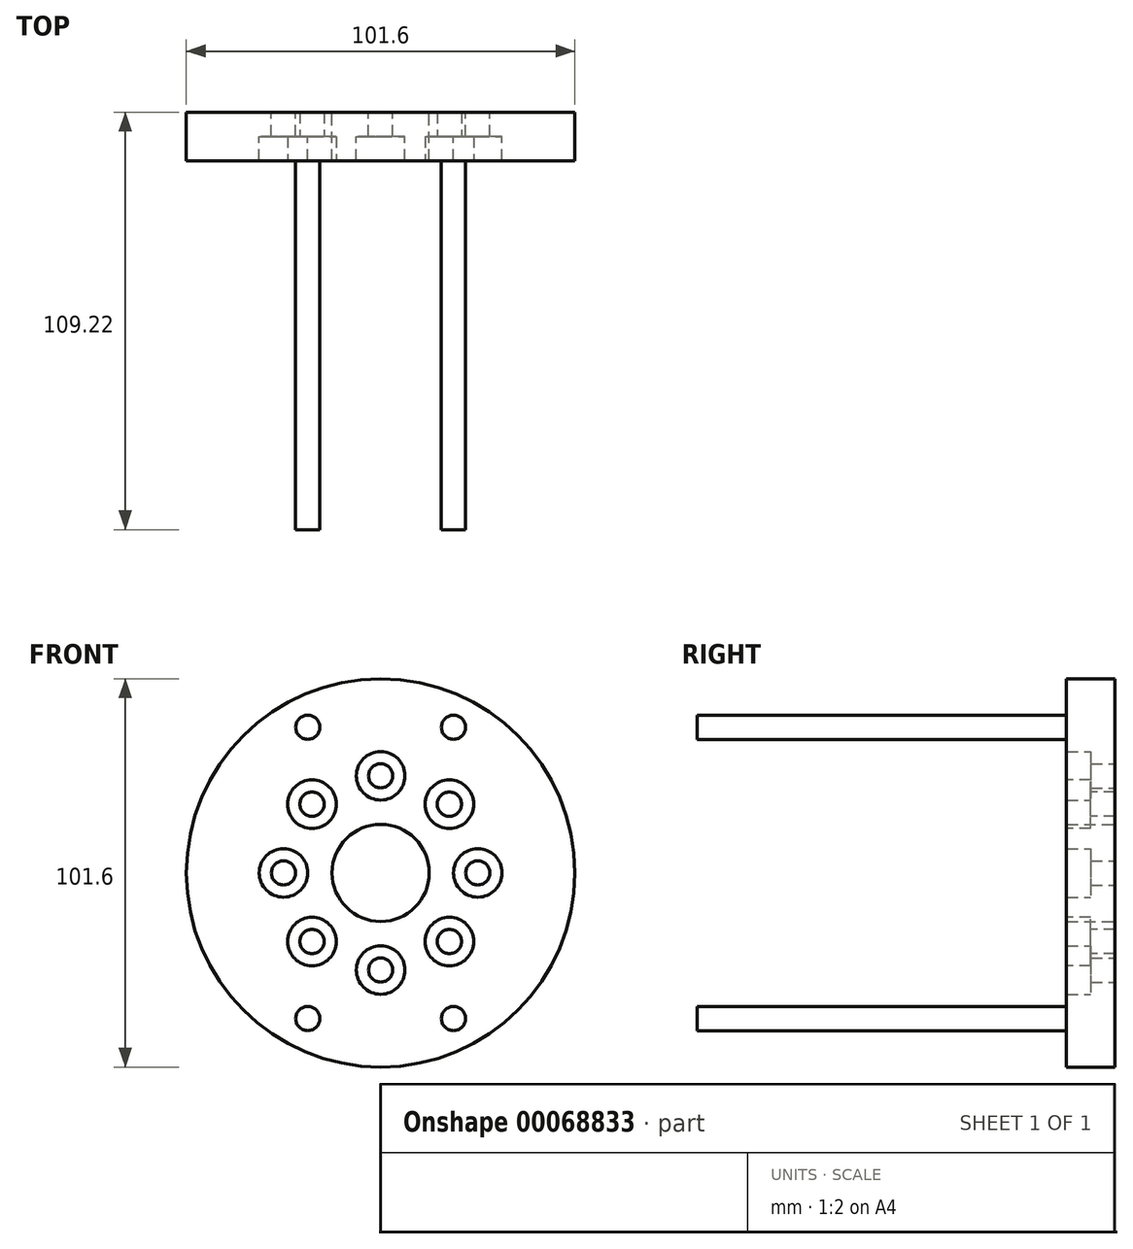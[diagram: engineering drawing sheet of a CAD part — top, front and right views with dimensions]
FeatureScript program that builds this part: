
annotation { "Feature Type Name" : "Feature", "Feature Type Description" : "" }
export const myFeature = defineFeature(function(context is Context, id is Id, definition is map)
    precondition{}
    {
        {
            var Q0;
            Q0=qCreatedBy(makeId("Front.planeOp"),FACE);
            var sketch = newSketch(context, id + "F0", { "sketchPlane" : qUnion([Q0])});
            skCircle(sketch, "E0", {"center": v(0, 0) * mm, "radius": 50.8 * mm});
            skCircle(sketch, "E1", {"center": v(0, 0) * mm, "radius": 12.7 * mm});
            skCircle(sketch, "E2", {"center": v(0, 0) * mm, "radius": 34.93 * mm, "construction": true});
            skPoint(sketch, "E3", {"position": v(0, 34.93) * mm});
            skPoint(sketch, "E4", {"position": v(-34.93, 0) * mm});
            skPoint(sketch, "E5", {"position": v(0, -34.92) * mm});
            skPoint(sketch, "E6", {"position": v(34.93, 0) * mm});
            skSolve(sketch);
        }
        {
            var Q0;
            Q0 = qSketchRegion(id + "F0", true);
            extrude(context, id + "F1", {"entities" : qUnion([Q0]), "depth" : 12.7 * mm});
        }
        {
            var Q0;
            Q0=makeQuery(id+"F1.opExtrude","CAP_FACE",FACE,{"disambiguationData":[OSD([sQuery(id+"F0.wireOp",EDGE,"E0")])],"isStart":false});
            var sketch = newSketch(context, id + "F2", { "sketchPlane" : qUnion([Q0])});
            skCircle(sketch, "E7", {"center": v(-17.96, 17.96) * mm, "radius": 6.35 * mm});
            skCircle(sketch, "E8", {"center": v(17.96, 17.96) * mm, "radius": 6.35 * mm});
            skCircle(sketch, "E9", {"center": v(17.96, -17.96) * mm, "radius": 6.35 * mm});
            skCircle(sketch, "E10", {"center": v(-17.96, -17.96) * mm, "radius": 6.35 * mm});
            skCircle(sketch, "E11", {"center": v(0, 0) * mm, "radius": 25.4 * mm, "construction": true});
            skLineSegment(sketch, "E12", {"start": v(0, 0) * mm, "end": v(-17.96, 17.96) * mm, "construction": true});
            skLineSegment(sketch, "E13", {"start": v(0, 0) * mm, "end": v(-25.4, 0) * mm, "construction": true});
            skPoint(sketch, "E14", {"position": v(0, 25.4) * mm});
            skPoint(sketch, "E15", {"position": v(-25.4, 0) * mm});
            skPoint(sketch, "E16", {"position": v(25.4, 0) * mm});
            skPoint(sketch, "E17", {"position": v(0, -25.4) * mm});
            skSolve(sketch);
        }
        {
            var Q0;
            Q0 = qSketchRegion(id + "F2", true);
            extrude(context, id + "F3", {"entities" : qUnion([Q0]), "operationType" : NewBodyOperationType.REMOVE, "oppositeDirection" : true, "depth" : 6.35 * mm});
        }
        {
            var Q0;
            Q0=sQuery(id+"F2.wireOp",VERTEX,"E14");
            var Q1;
            Q1=sQuery(id+"F2.wireOp",VERTEX,"E15");
            var Q2;
            Q2=sQuery(id+"F2.wireOp",VERTEX,"E17");
            var Q3;
            Q3=sQuery(id+"F2.wireOp",VERTEX,"E16");
            var Q4;
            Q4=makeQuery(id+"F1.opExtrude","SWEPT_BODY",BODY,{"disambiguationData":[OSD([sQuery(id+"F0.wireOp",EDGE,"E0"),sQuery(id+"F0.wireOp",EDGE,"E1")])]});
            hole(context, id + "F4", {"style" : HoleStyle.C_BORE, "holeDiameter" : 6.35 * mm, "cBoreDiameter" : 12.7 * mm, "cBoreDepth" : 6.35 * mm, "endStyle" : HoleEndStyle.THROUGH, "locations" : qUnion([Q0, Q1, Q2, Q3]), "scope" : qUnion([Q4])});
        }
        {
            var Q0;
            Q0=makeQuery(id+"F1.opExtrude","CAP_FACE",FACE,{"disambiguationData":[OSD([sQuery(id+"F0.wireOp",EDGE,"E0"),sQuery(id+"F0.wireOp",EDGE,"E1")])],"isStart":false});
            var sketch = newSketch(context, id + "F5", { "sketchPlane" : qUnion([Q0])});
            skCircle(sketch, "E18", {"center": v(-19.05, 38.1) * mm, "radius": 3.18 * mm});
            skCircle(sketch, "E19", {"center": v(19.05, 38.1) * mm, "radius": 3.18 * mm});
            skCircle(sketch, "E20", {"center": v(19.05, -38.1) * mm, "radius": 3.18 * mm});
            skCircle(sketch, "E21", {"center": v(-19.05, -38.1) * mm, "radius": 3.18 * mm});
            skLineSegment(sketch, "E22.bottom", {"start": v(-19.05, -38.1) * mm, "end": v(19.05, -38.1) * mm, "construction": true});
            skLineSegment(sketch, "E22.top", {"start": v(-19.05, 38.1) * mm, "end": v(19.05, 38.1) * mm, "construction": true});
            skLineSegment(sketch, "E22.left", {"start": v(-19.05, -38.1) * mm, "end": v(-19.05, 38.1) * mm, "construction": true});
            skLineSegment(sketch, "E22.right", {"start": v(19.05, -38.1) * mm, "end": v(19.05, 38.1) * mm, "construction": true});
            skSolve(sketch);
        }
        {
            var Q0;
            Q0 = qSketchRegion(id + "F5", true);
            extrude(context, id + "F6", {"entities" : qUnion([Q0]), "operationType" : NewBodyOperationType.ADD, "depth" : 96.52 * mm});
        }
        {
            var Q0;
            Q0=makeQuery(id+"F3.boolean.opBoolean","COPY",FACE,{"derivedFrom":makeQuery(id+"F3.opExtrude","CAP_FACE",FACE,{"disambiguationData":[OSD([sQuery(id+"F2.wireOp",EDGE,"E7")])],"isStart":false})});
            var sketch = newSketch(context, id + "F7", { "sketchPlane" : qUnion([Q0])});
            skCircle(sketch, "E23", {"center": v(-17.96, 17.96) * mm, "radius": 3.18 * mm});
            skCircle(sketch, "E24.0.1.0", {"center": v(-17.96, -17.96) * mm, "radius": 3.18 * mm});
            skCircle(sketch, "E24.1.0.0", {"center": v(17.96, 17.96) * mm, "radius": 3.18 * mm});
            skCircle(sketch, "E24.1.1.0", {"center": v(17.96, -17.96) * mm, "radius": 3.18 * mm});
            skLineSegment(sketch, "E24.direction1", {"start": v(-17.96, 17.96) * mm, "end": v(17.96, 17.96) * mm, "construction": true});
            skLineSegment(sketch, "E24.direction2", {"start": v(-17.96, 17.96) * mm, "end": v(-17.96, -17.96) * mm, "construction": true});
            skSolve(sketch);
        }
        {
            var Q0;
            Q0 = qSketchRegion(id + "F7", true);
            extrude(context, id + "F8", {"entities" : qUnion([Q0]), "operationType" : NewBodyOperationType.REMOVE, "oppositeDirection" : true, "depth" : 25.4 * mm});
        }
    });
